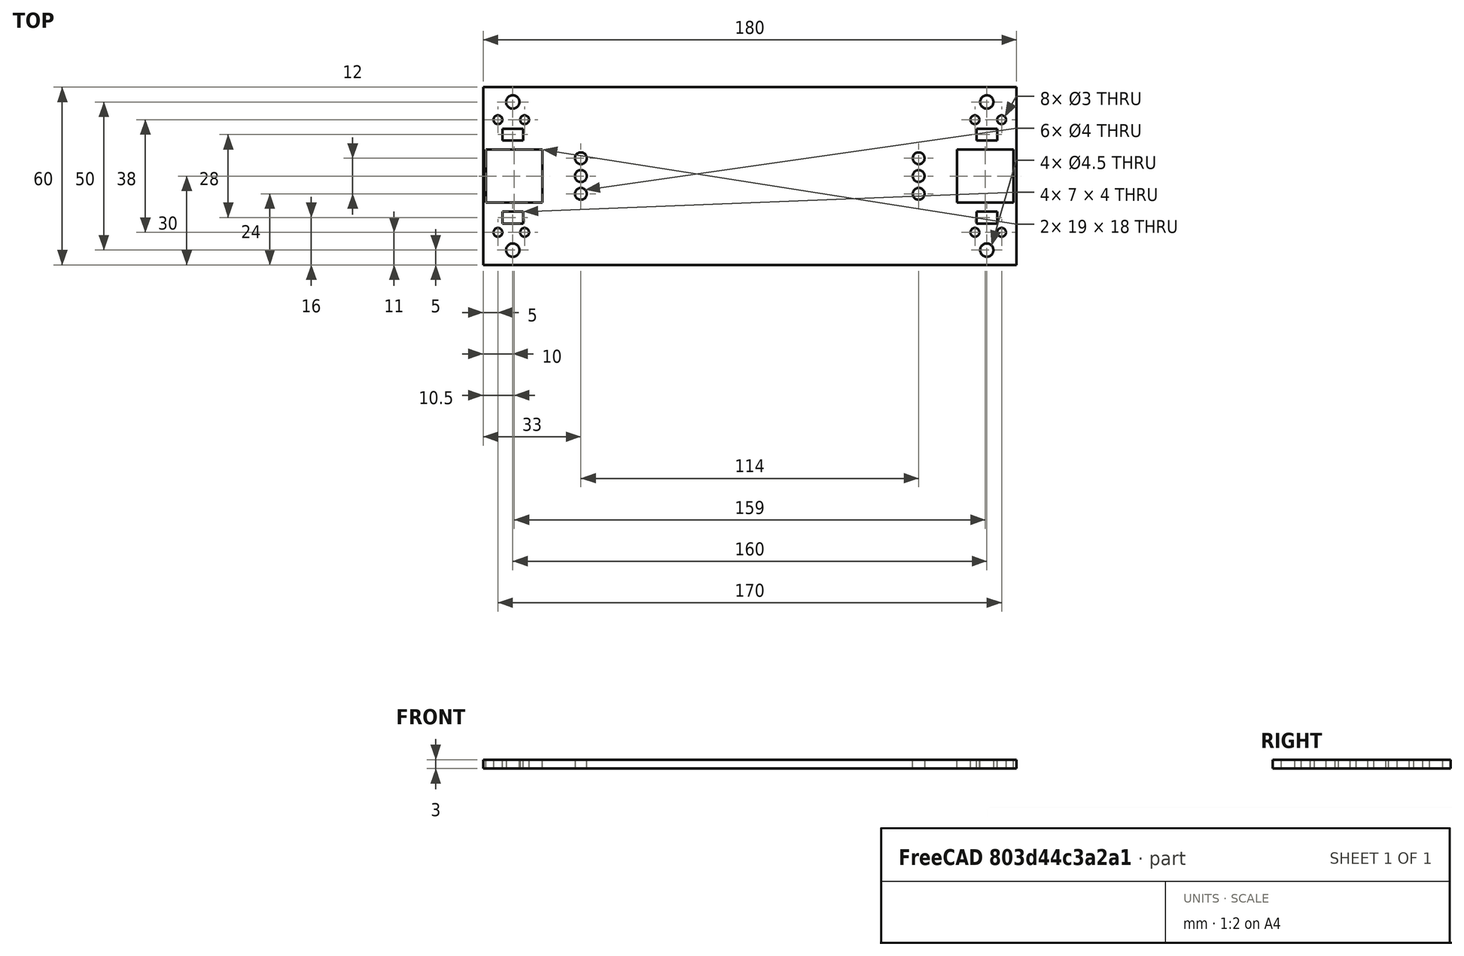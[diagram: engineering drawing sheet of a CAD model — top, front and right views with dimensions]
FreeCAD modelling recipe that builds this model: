
FCSTD DOCUMENT  (FreeCAD 0.16R6707 (Git))
Label: support_support_guidage_horizontal
License: All rights reserved
LicenseURL: http://en.wikipedia.org/wiki/All_rights_reserved
objects: Sketcher::SketchObject×1, PartDesign::Pad×1, PartDesign::Mirrored×1
note: 4 computed .brp shape members not serialized (recipe doc carries the construction recipe); baked Part::Feature solids carry a one-line shape summary decoded from their .brp

FEATURE [Sketcher::SketchObject] Sketch
  sketch-geometry (41):
    g0: LineSegment StartX=0 StartY=0 StartZ=0 EndX=90 EndY=0 EndZ=0
    g1: LineSegment StartX=0 StartY=60 StartZ=0 EndX=0 EndY=0 EndZ=0
    g2: GeomPoint [constr] X=10 Y=5 Z=0
    g3: GeomPoint [constr] X=6.5 Y=14 Z=0
    g4: Circle CenterX=10 CenterY=5 CenterZ=0 NormalX=0 NormalY=0 NormalZ=1 Radius=2.25
    g5: GeomPoint [constr] X=33 Y=30 Z=0
    g6: GeomPoint [constr] X=33 Y=24 Z=0
    g7: Circle CenterX=33 CenterY=24 CenterZ=0 NormalX=0 NormalY=0 NormalZ=1 Radius=2
    g8: LineSegment StartX=6.5 StartY=14 StartZ=0 EndX=13.5 EndY=14 EndZ=0
    g9: LineSegment StartX=13.5 StartY=14 StartZ=0 EndX=13.5 EndY=18 EndZ=0
    g10: LineSegment StartX=13.5 StartY=18 StartZ=0 EndX=6.5 EndY=18 EndZ=0
    g11: LineSegment StartX=6.5 StartY=18 StartZ=0 EndX=6.5 EndY=14 EndZ=0
    g12: LineSegment StartX=90 StartY=0 StartZ=0 EndX=90 EndY=60 EndZ=0
    g13: GeomPoint [constr] X=33 Y=36 Z=0
    g14: Circle CenterX=33 CenterY=36 CenterZ=0 NormalX=0 NormalY=0 NormalZ=1 Radius=2
    g15: Circle CenterX=33 CenterY=30 CenterZ=0 NormalX=0 NormalY=0 NormalZ=1 Radius=2
    g16: LineSegment StartX=0 StartY=60 StartZ=0 EndX=90 EndY=60 EndZ=0
    g17: GeomPoint [constr] X=6.5 Y=46 Z=0
    g18: LineSegment StartX=6.5 StartY=46 StartZ=0 EndX=13.5 EndY=46 EndZ=0
    g19: LineSegment StartX=13.5 StartY=46 StartZ=0 EndX=13.5 EndY=42 EndZ=0
    g20: LineSegment StartX=13.5 StartY=42 StartZ=0 EndX=6.5 EndY=42 EndZ=0
    g21: LineSegment StartX=6.5 StartY=42 StartZ=0 EndX=6.5 EndY=46 EndZ=0
    g22: GeomPoint [constr] X=10 Y=55 Z=0
    g23: Circle CenterX=10 CenterY=55 CenterZ=0 NormalX=0 NormalY=0 NormalZ=1 Radius=2.25
    g24: GeomPoint [constr] X=20 Y=49 Z=0
    g25: GeomPoint [constr] X=20 Y=11 Z=0
    g26: GeomPoint [constr] X=23 Y=11 Z=0
    g27: GeomPoint [constr] X=23 Y=49 Z=0
    g28: GeomPoint [constr] X=14 Y=49 Z=0
    g29: GeomPoint [constr] X=5 Y=49 Z=0
    g30: GeomPoint [constr] X=14 Y=11 Z=0
    g31: GeomPoint [constr] X=5 Y=11 Z=0
    g32: Circle CenterX=14 CenterY=11 CenterZ=0 NormalX=0 NormalY=0 NormalZ=1 Radius=1.5
    g33: Circle CenterX=5 CenterY=11 CenterZ=0 NormalX=0 NormalY=0 NormalZ=1 Radius=1.5
    g34: Circle CenterX=14 CenterY=49 CenterZ=0 NormalX=0 NormalY=0 NormalZ=1 Radius=1.5
    g35: Circle CenterX=5 CenterY=49 CenterZ=0 NormalX=0 NormalY=0 NormalZ=1 Radius=1.5
    g36: GeomPoint [constr] X=20 Y=39 Z=0
    g37: LineSegment StartX=20 StartY=39 StartZ=0 EndX=1 EndY=39 EndZ=0
    g38: LineSegment StartX=1 StartY=39 StartZ=0 EndX=1 EndY=21 EndZ=0
    g39: LineSegment StartX=1 StartY=21 StartZ=0 EndX=20 EndY=21 EndZ=0
    g40: LineSegment StartX=20 StartY=21 StartZ=0 EndX=20 EndY=39 EndZ=0
  constraints (94):
    c: Coincident(g1,g0)
    c: Horizontal(g0)
    c: Vertical(g1)
    c: Coincident(g0,g-1)
    c: Distance(g1) = 60
    c: Distance(g0) = 90
    c: DistanceY(g2) = 5
    c: DistanceX(g2) = 10
    c: Coincident(g4,g2)
    c: Radius(g4) = 2.25
    c: DistanceX(g3) = 6.5
    c: DistanceY(g3) = 14
    c: DistanceY(g5) = 30
    c: DistanceX(g5) = 33
    c: DistanceY(g6,g5) = 6
    c: DistanceX(g5,g6) = 0
    c: Coincident(g7,g6)
    c: Coincident(g8,g9)
    c: Coincident(g9,g10)
    c: Coincident(g10,g11)
    c: Coincident(g11,g8)
    c: Horizontal(g8)
    c: Horizontal(g10)
    c: Vertical(g9)
    c: Vertical(g11)
    c: Coincident(g8,g3)
    c: Distance(g10) = 7
    c: Distance(g9) = 4
    c: Coincident(g12,g0)
    c: Vertical(g12)
    c: DistanceY(g5,g13) = 6
    c: DistanceX(g5,g13) = 0
    c: Coincident(g14,g13)
    c: Coincident(g15,g5)
    c: Radius(g15) = 2
    c: Equal(g15,g14)
    c: Equal(g15,g7)
    c: Coincident(g16,g1)
    c: Coincident(g16,g12)
    c: Horizontal(g16)
    c: DistanceX(g3,g17) = 0
    c: Coincident(g18,g19)
    c: Coincident(g19,g20)
    c: Coincident(g20,g21)
    c: Coincident(g21,g18)
    c: Horizontal(g18)
    c: Horizontal(g20)
    c: Vertical(g19)
    c: Vertical(g21)
    c: Coincident(g18,g17)
    c: Distance(g18) = 7
    c: Distance(g19) = 4
    c: DistanceY(g22,g1) = 5
    c: DistanceX(g22) = 10
    c: DistanceY(g17,g1) = 14
    c: Coincident(g23,g22)
    c: Radius(g23) = 2.25
    c: DistanceX(g24) = 20
    c: DistanceX(g24,g25) = 0
    c: DistanceY(g25) = 11
    c: DistanceY(g24,g1) = 11
    c: DistanceY(g25,g26) = 0
    c: DistanceX(g25,g26) = 3
    c: DistanceY(g24,g27) = 0
    c: DistanceX(g24,g27) = 3
    c: DistanceY(g27,g28) = 0
    c: DistanceY(g28,g29) = 0
    c: DistanceX(g28,g29) = -9
    c: DistanceY(g26,g30) = 0
    c: DistanceY(g31,g30) = 0
    c: DistanceX(g30,g31) = -9
    c: Coincident(g32,g30)
    c: Coincident(g33,g31)
    c: Coincident(g34,g28)
    c: Coincident(g35,g29)
    c: Radius(g34) = 1.5
    c: Equal(g34,g35)
    c: Equal(g34,g33)
    c: Equal(g34,g32)
    c: DistanceX(g25,g30) = -6
    c: DistanceX(g24,g28) = -6
    c: DistanceX(g36,g24) = 0
    c: DistanceY(g13,g36) = 3
    c: Coincident(g37,g38)
    c: Coincident(g38,g39)
    c: Coincident(g39,g40)
    c: Coincident(g40,g37)
    c: Horizontal(g37)
    c: Horizontal(g39)
    c: Vertical(g38)
    c: Vertical(g40)
    c: Coincident(g37,g36)
    c: Distance(g37) = 19
    c: Distance(g38) = 18
FEATURE [PartDesign::Pad] Pad
  Length = 3
  Length2 = 100
  Sketch = -> Sketch
  Type = 0
FEATURE [PartDesign::Mirrored] Mirrored
  MirrorPlane = -> Pad [Face2]
  Originals = -> [Pad]
